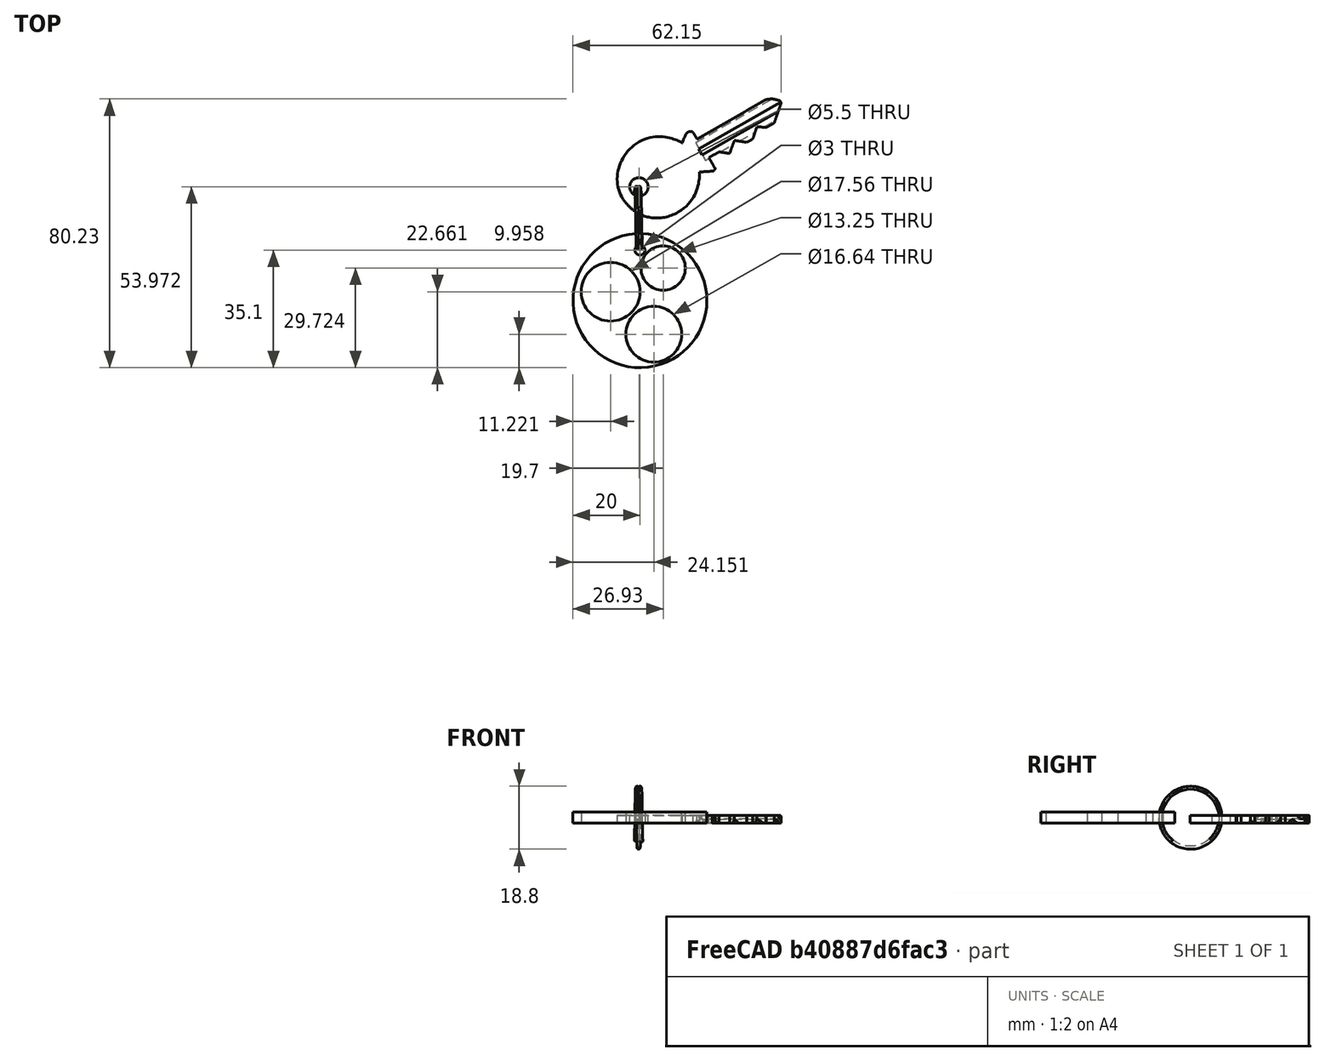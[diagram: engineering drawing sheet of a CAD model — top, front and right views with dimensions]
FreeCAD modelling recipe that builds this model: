
FCSTD DOCUMENT  (FreeCAD 0.17R13509 (Git))
Label: T5-ej1
License: CreativeCommons Attribution-ShareAlike
LicenseURL: http://creativecommons.org/licenses/by-sa/4.0/
objects: Sketcher::SketchObject×2, Part::Feature×2, PartDesign::Pocket×2, Part::Cylinder×1, App::DocumentObjectGroup×1, PartDesign::FeatureBase×1, PartDesign::Body×1, App::Part×1
note: 11 computed .brp shape members not serialized (recipe doc carries the construction recipe); baked Part::Feature solids carry a one-line shape summary decoded from their .brp

FEATURE [Part::Cylinder] Cylinder  label="casino-chip-main body"
  Angle = 360
  AttacherType = Attacher::AttachEngine3D
  Height = 3.3
  Radius = 20
FEATURE [Sketcher::SketchObject] Sketch  label="hole-sketch"
  MapMode = 5
  Placement = pos=(0,0,3.3) rot=(0,0,1;0rad)
  Support = -> [Cylinder]
  sketch-geometry (1):
    g0: Circle CenterX=0 CenterY=15.1 CenterZ=0 NormalX=0 NormalY=0 NormalZ=1 AngleXU=0 Radius=1.5
  constraints (3):
    c: Radius(g0) = 1.5
    c: PointOnObject(g0,g-2)
    c: DistanceY(g-1,g0) = 15.1
FEATURE [App::DocumentObjectGroup] Group001  label="Casino-chip-src"
  Group = -> [Cylinder]
FEATURE [Part::Feature] Sweep  label="key-ring-model-1"
  Placement = pos=(-1.2,24.7546,1.6391) rot=(0.333333,0.881918,0.333333;1.69612rad)
  shape: bbox 3.31 x 27.02 x 26.33 mm, 4 faces (baked)
FEATURE [Part::Feature] Cut  label="key-model-1"
  Placement = pos=(-5.46976,31.0266,0) rot=(0,0,1;0.517888rad)
  shape: bbox 49.82 x 36.6 x 2.3 mm, 44 faces (baked)
FEATURE [PartDesign::FeatureBase] BaseFeature
  BaseFeature = -> Cylinder
FEATURE [PartDesign::Pocket] Pocket  label="casino-chip-key-chain"
  BaseFeature = -> BaseFeature
  Length = 5
  Length2 = 100
  Profile = -> Sketch
  Type = 1
FEATURE [Sketcher::SketchObject] Sketch001
  MapMode = 5
  Support = -> [XY_Plane001]
  sketch-geometry (3):
    g0: Circle CenterX=-8.77867 CenterY=2.66139 CenterZ=0 NormalX=0 NormalY=0 NormalZ=1 AngleXU=0 Radius=8.77867
    g1: Circle CenterX=6.92987 CenterY=9.72424 CenterZ=0 NormalX=0 NormalY=0 NormalZ=1 AngleXU=0 Radius=6.62593
    g2: Circle CenterX=4.15069 CenterY=-10.0417 CenterZ=0 NormalX=0 NormalY=0 NormalZ=1 AngleXU=0 Radius=8.32048
  constraints (1):
    c: Tangent(g0,g-2)
FEATURE [PartDesign::Pocket] Pocket001
  BaseFeature = -> Pocket
  Length = 5
  Length2 = 100
  Profile = -> Sketch001
  Reversed = true
  Type = 1
FEATURE [PartDesign::Body] PocketBody
  BaseFeature = -> Cylinder
  Group = -> [BaseFeature,Sketch,Pocket,Sketch001,Pocket001]
  Origin = -> Origin001
  Tip = -> Pocket001
FEATURE [App::Part] Part
  Group = -> [PocketBody]
  License = CC BY 3.0
  LicenseURL = http://creativecommons.org/licenses/by/3.0/
  Origin = -> Origin
